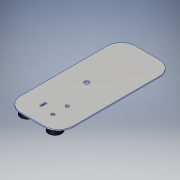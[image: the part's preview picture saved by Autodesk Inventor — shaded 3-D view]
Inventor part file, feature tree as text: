
AUTODESK INVENTOR PART (.ipt)
format: ipt  version: 2018 (Build 220112000, 112)  size: 201,728 bytes
history: native  units: in
note: dims shown in document units (in); Inventor stores cm internally (conversion verified against a paired STEP export)
features: extrude x4, sketch x4
ambient origin geometry x8: Origin, YZ Plane, XZ Plane, XY Plane, X Axis, Y Axis, Z Axis, Center Point
bodies: Solid1 (feature_tree)
feature tree (8):
  extrude  "Extrusion1"  Depth=0.5in
  extrude  "Extrusion2"  Depth=0.5in
  extrude  "Extrusion3"  Depth=0.5in
  extrude  "Extrusion4"  Depth=0.5in
  sketch  "Sketch1"  dims[d1=3.999in d2=0.5in]
  sketch  "Sketch2"  dims[d3=0.5in d4=0.5in]
  sketch  "Sketch3"  dims[d5=0.5in d6=0.5in]
  sketch  "Sketch4"  dims[d7=0.5in d8=0.5in d9=0.5in d10=1.82in d11=0.75in d12=1.95in d13=0.158in d14=0.058in d15=0.534in d16=0.192in d17=0.625in d18=0.5in d19=0.7in d20=0.5in d21=0.111in d22=0.111in d23=0.0385in d24=0.0in d25=0.425in d26=0.3in d27=0.45in d28=0.425in d29=0.45in d30=0.3in d31=0.45in d32=0.45in d33=0.05in d34=0.084in d35=0.2in d36=0.0in d37=0.025in d38=0.058in d39=0.029in d40=0.125in d41=0.0in d42=0.096in d43=0.192in d44=0.0625in d45=0.125in d46=0.075in d47=0.125in d48=0.0in]
